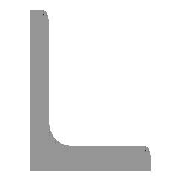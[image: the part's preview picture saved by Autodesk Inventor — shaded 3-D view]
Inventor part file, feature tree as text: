
AUTODESK INVENTOR PART (.ipt)
format: ipt  version: 2023.5 (Build 275446000, 446)  size: 137,216 bytes
history: native  units: mm (DEFAULTED — no unit token found)
features: other x3, sketch x2, hole x1, plane x1, projected_geometry x1
ambient origin geometry x8: Origin, YZ Plane, XZ Plane, XY Plane, X Axis, Y Axis, Z Axis, Center Point
bodies: Solid1 (feature_tree), Body (feature_tree)
feature tree (8):
  other  "Driven Length"
  other  "Start plane"
  other  "End plane"
  hole  "Hole1"  [1 undecoded]
  sketch  "Sketch3"  dims[d0=25.4mm d1=25.4mm]
  plane  "Work Plane3"
  sketch  "Sketch5"  dims[d2=3.175mm d3=3.175mm d4=50.8mm d5=0.0mm d10=0.0mm d11=0.0mm d12=-0.0mm d13=50.8mm d14=3.302mm d15=1.524mm d16=90.0deg d17=50.8mm d18=25.4mm d19=5.1054mm d20=9.652mm d21=9.779mm d22=6.35mm d23=14.3117mm d24=25.4mm d25=20.594885mm]
  projected_geometry  "Projected Loop2"
note: 1 required parameter value undecoded (feature->parameter linkage not recoverable at this tier; creation-order binding heuristic only, values carry confidence <= 0.55)
